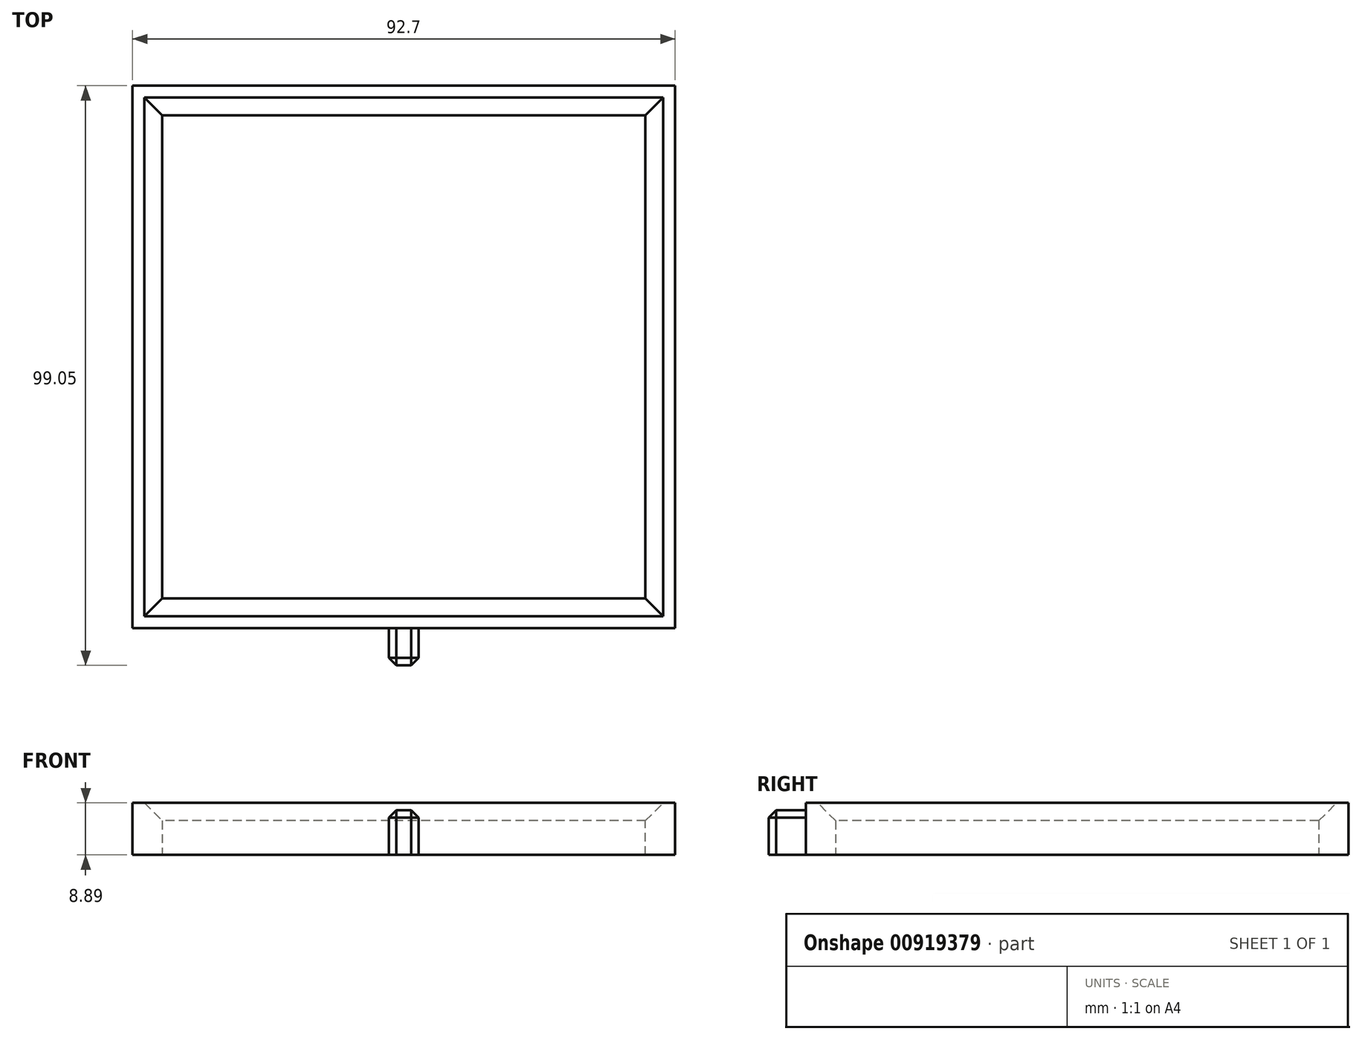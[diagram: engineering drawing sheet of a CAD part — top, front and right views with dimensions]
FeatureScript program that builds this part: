
annotation { "Feature Type Name" : "Feature", "Feature Type Description" : "" }
export const myFeature = defineFeature(function(context is Context, id is Id, definition is map)
    precondition{}
    {
        {
            var Q0;
            Q0=qCreatedBy(makeId("Front.planeOp"),FACE);
            var sketch = newSketch(context, id + "F0", { "sketchPlane" : qUnion([Q0])});
            skLineSegment(sketch, "E0", {"start": v(0, 0) * mm, "end": v(-41.28, 0) * mm});
            skLineSegment(sketch, "E1", {"start": v(0, 0) * mm, "end": v(41.28, 0) * mm});
            skLineSegment(sketch, "E2.bottom", {"start": v(-41.28, 0) * mm, "end": v(41.28, 0) * mm});
            skLineSegment(sketch, "E2.top", {"start": v(-41.28, -3.8) * mm, "end": v(41.28, -3.8) * mm});
            skLineSegment(sketch, "E2.left", {"start": v(-41.28, 0) * mm, "end": v(-41.28, -3.8) * mm});
            skLineSegment(sketch, "E2.right", {"start": v(41.28, 0) * mm, "end": v(41.28, -3.8) * mm});
            skLineSegment(sketch, "E3.bottom", {"start": v(-41.28, -3.8) * mm, "end": v(-46.35, -3.8) * mm});
            skLineSegment(sketch, "E3.top", {"start": v(-41.28, 5.08) * mm, "end": v(-46.36, 5.08) * mm});
            skLineSegment(sketch, "E3.left", {"start": v(-41.28, -3.8) * mm, "end": v(-41.28, 5.08) * mm});
            skLineSegment(sketch, "E3.right", {"start": v(-46.35, -3.8) * mm, "end": v(-46.35, 5.08) * mm});
            skLineSegment(sketch, "E4.bottom", {"start": v(41.28, -3.8) * mm, "end": v(46.36, -3.8) * mm});
            skLineSegment(sketch, "E4.top", {"start": v(41.28, 5.08) * mm, "end": v(46.36, 5.08) * mm});
            skLineSegment(sketch, "E4.left", {"start": v(41.28, -3.8) * mm, "end": v(41.28, 5.08) * mm});
            skLineSegment(sketch, "E4.right", {"start": v(46.36, -3.8) * mm, "end": v(46.36, 5.08) * mm});
            skSolve(sketch);
        }
        {
            var Q0;
            {var subQ3=sQuery(id+"F0.wireOp",EDGE,"E3.bottom");Q0=makeQuery(id+"F0.imprint","IMPRINT",FACE,{"disambiguationData":[TD([[makeQuery(id+"F0.imprint","IMPRINT",EDGE,{"derivedFrom":subQ3}),-1.0]])]});}
            var Q1;
            {var subQ0=sQuery(id+"F0.wireOp",EDGE,"E2.bottom");Q1=makeQuery(id+"F0.imprint","IMPRINT",FACE,{"disambiguationData":[TD([[makeQuery(id+"F0.imprint","IMPRINT",EDGE,{"derivedFrom":subQ0}),-1.0]])]});}
            var Q2;
            {var subQ3=sQuery(id+"F0.wireOp",EDGE,"E4.bottom");Q2=makeQuery(id+"F0.imprint","IMPRINT",FACE,{"disambiguationData":[TD([[makeQuery(id+"F0.imprint","IMPRINT",EDGE,{"derivedFrom":subQ3}),1.0]])]});}
            extrude(context, id + "F1", {"entities" : qUnion([Q0, Q1, Q2]), "endBound" : BoundingType.SYMMETRIC, "depth" : 82.55 * mm, "offsetDistance" : 25.4 * mm});
        }
        {
            var Q0;
            Q0=makeQuery(id+"F1.opExtrude","CAP_FACE",FACE,{"disambiguationData":[OSD([sQuery(id+"F0.wireOp",EDGE,"E2.bottom"),sQuery(id+"F0.wireOp",EDGE,"E2.top"),sQuery(id+"F0.wireOp",EDGE,"E3.bottom"),sQuery(id+"F0.wireOp",EDGE,"E3.top"),sQuery(id+"F0.wireOp",EDGE,"E3.left"),sQuery(id+"F0.wireOp",EDGE,"E3.right"),sQuery(id+"F0.wireOp",EDGE,"E4.bottom"),sQuery(id+"F0.wireOp",EDGE,"E4.top"),sQuery(id+"F0.wireOp",EDGE,"E4.left"),sQuery(id+"F0.wireOp",EDGE,"E4.right")])],"isStart":true});
            var sketch = newSketch(context, id + "F2", { "sketchPlane" : qUnion([Q0])});
            skLineSegment(sketch, "E5.bottom", {"start": v(-46.36, -3.8) * mm, "end": v(46.36, -3.8) * mm});
            skLineSegment(sketch, "E5.top", {"start": v(-46.36, 5.08) * mm, "end": v(46.36, 5.08) * mm});
            skLineSegment(sketch, "E5.left", {"start": v(-46.36, -3.8) * mm, "end": v(-46.36, 5.08) * mm});
            skLineSegment(sketch, "E5.right", {"start": v(46.36, -3.8) * mm, "end": v(46.36, 5.08) * mm});
            skSolve(sketch);
        }
        {
            var Q0;
            Q0=makeQuery(id+"F2.imprint","IMPRINT",FACE,{"disambiguationData":[TD([[makeQuery(id+"F2.imprint","IMPRINT",EDGE,{"derivedFrom":makeQuery(id+"F1.opExtrude","CAP_EDGE",EDGE,{"disambiguationData":[OSD([sQuery(id+"F0.wireOp",EDGE,"E2.bottom")])],"isStart":true})}),-1.0]])]});
            var Q1;
            Q1=makeQuery(id+"F2.imprint","IMPRINT",FACE,{"disambiguationData":[TD([[makeQuery(id+"F2.imprint","IMPRINT",EDGE,{"derivedFrom":sQuery(id+"F2.wireOp",EDGE,"E5.bottom")}),1.0]])]});
            extrude(context, id + "F3", {"entities" : qUnion([Q0, Q1]), "operationType" : NewBodyOperationType.ADD, "depth" : 5.08 * mm, "offsetDistance" : 25.4 * mm});
        }
        {
            var Q0;
            Q0=makeQuery(id+"F1.opExtrude","CAP_FACE",FACE,{"disambiguationData":[OSD([sQuery(id+"F0.wireOp",EDGE,"E2.bottom"),sQuery(id+"F0.wireOp",EDGE,"E2.top"),sQuery(id+"F0.wireOp",EDGE,"E3.bottom"),sQuery(id+"F0.wireOp",EDGE,"E3.top"),sQuery(id+"F0.wireOp",EDGE,"E3.left"),sQuery(id+"F0.wireOp",EDGE,"E3.right"),sQuery(id+"F0.wireOp",EDGE,"E4.bottom"),sQuery(id+"F0.wireOp",EDGE,"E4.top"),sQuery(id+"F0.wireOp",EDGE,"E4.left"),sQuery(id+"F0.wireOp",EDGE,"E4.right")])],"isStart":false});
            var sketch = newSketch(context, id + "F4", { "sketchPlane" : qUnion([Q0])});
            skLineSegment(sketch, "E6.bottom", {"start": v(-46.36, -3.8) * mm, "end": v(46.36, -3.8) * mm});
            skLineSegment(sketch, "E6.top", {"start": v(-46.36, 5.08) * mm, "end": v(46.36, 5.08) * mm});
            skLineSegment(sketch, "E6.left", {"start": v(-46.35, -3.8) * mm, "end": v(-46.35, 5.08) * mm});
            skLineSegment(sketch, "E6.right", {"start": v(46.36, -3.8) * mm, "end": v(46.36, 5.08) * mm});
            skSolve(sketch);
        }
        {
            var Q0;
            Q0 = qSketchRegion(id + "F4", true);
            extrude(context, id + "F5", {"entities" : qUnion([Q0]), "operationType" : NewBodyOperationType.ADD, "depth" : 5.08 * mm, "offsetDistance" : 25.4 * mm});
        }
        {
            var Q0;
            Q0=makeQuery(id+"F5.opExtrude","CAP_FACE",FACE,{"disambiguationData":[OSD([sQuery(id+"F4.wireOp",EDGE,"E6.bottom"),sQuery(id+"F4.wireOp",EDGE,"E6.top"),sQuery(id+"F4.wireOp",EDGE,"E6.left"),sQuery(id+"F4.wireOp",EDGE,"E6.right")])],"isStart":false});
            var sketch = newSketch(context, id + "F6", { "sketchPlane" : qUnion([Q0])});
            skLineSegment(sketch, "E7.bottom", {"start": v(2.54, -3.8) * mm, "end": v(-2.54, -3.8) * mm});
            skLineSegment(sketch, "E7.top", {"start": v(2.54, 3.8) * mm, "end": v(-2.54, 3.8) * mm});
            skLineSegment(sketch, "E7.left", {"start": v(2.54, -3.8) * mm, "end": v(2.54, 3.8) * mm});
            skLineSegment(sketch, "E7.right", {"start": v(-2.54, -3.8) * mm, "end": v(-2.54, 3.8) * mm});
            skPoint(sketch, "E7.middle", {"position": v(0, 0) * mm});
            skSolve(sketch);
        }
        {
            var Q0;
            Q0 = qSketchRegion(id + "F6", true);
            extrude(context, id + "F7", {"entities" : qUnion([Q0]), "operationType" : NewBodyOperationType.ADD, "depth" : 6.35 * mm, "offsetDistance" : 25.4 * mm});
        }
        {
            var Q0;
            Q0=makeQuery(id+"F7.opExtrude","SWEPT_EDGE",EDGE,{"disambiguationData":[OSD([sQuery(id+"F6.wireOp",EDGE,"E7.top"),sQuery(id+"F6.wireOp",EDGE,"E7.right")])]});
            var Q1;
            Q1=makeQuery(id+"F7.opExtrude","SWEPT_EDGE",EDGE,{"disambiguationData":[OSD([sQuery(id+"F6.wireOp",EDGE,"E7.top"),sQuery(id+"F6.wireOp",EDGE,"E7.left")])]});
            var Q2;
            Q2=makeQuery(id+"F7.opExtrude","CAP_EDGE",EDGE,{"disambiguationData":[OSD([sQuery(id+"F6.wireOp",EDGE,"E7.top")])],"isStart":false});
            var Q3;
            Q3=makeQuery(id+"F7.opExtrude","CAP_EDGE",EDGE,{"disambiguationData":[OSD([sQuery(id+"F6.wireOp",EDGE,"E7.left")])],"isStart":false});
            var Q4;
            Q4=makeQuery(id+"F7.opExtrude","CAP_EDGE",EDGE,{"disambiguationData":[OSD([sQuery(id+"F6.wireOp",EDGE,"E7.right")])],"isStart":false});
            chamfer(context, id + "F8", {"entities" : qUnion([Q0, Q1, Q2, Q3, Q4]), "width" : 1.27 * mm, "tangentPropagation" : true});
        }
        {
            var Q0;
            Q0=makeQuery(id+"F1.opExtrude","SWEPT_EDGE",EDGE,{"disambiguationData":[OSD([sQuery(id+"F0.wireOp",EDGE,"E3.top"),sQuery(id+"F0.wireOp",EDGE,"E3.left")])]});
            var Q1;
            Q1=makeQuery(id+"F5.opExtrude","CAP_EDGE",EDGE,{"disambiguationData":[OSD([sQuery(id+"F4.wireOp",EDGE,"E6.top")])],"isStart":true});
            var Q2;
            Q2=makeQuery(id+"F3.opExtrude","CAP_EDGE",EDGE,{"disambiguationData":[OSD([sQuery(id+"F2.wireOp",EDGE,"E5.top")])],"isStart":true});
            var Q3;
            Q3=makeQuery(id+"F1.opExtrude","SWEPT_EDGE",EDGE,{"disambiguationData":[OSD([sQuery(id+"F0.wireOp",EDGE,"E4.top"),sQuery(id+"F0.wireOp",EDGE,"E4.left")])]});
            chamfer(context, id + "F9", {"entities" : qUnion([Q0, Q1, Q2, Q3]), "width" : 3.05 * mm, "tangentPropagation" : true});
        }
    });
